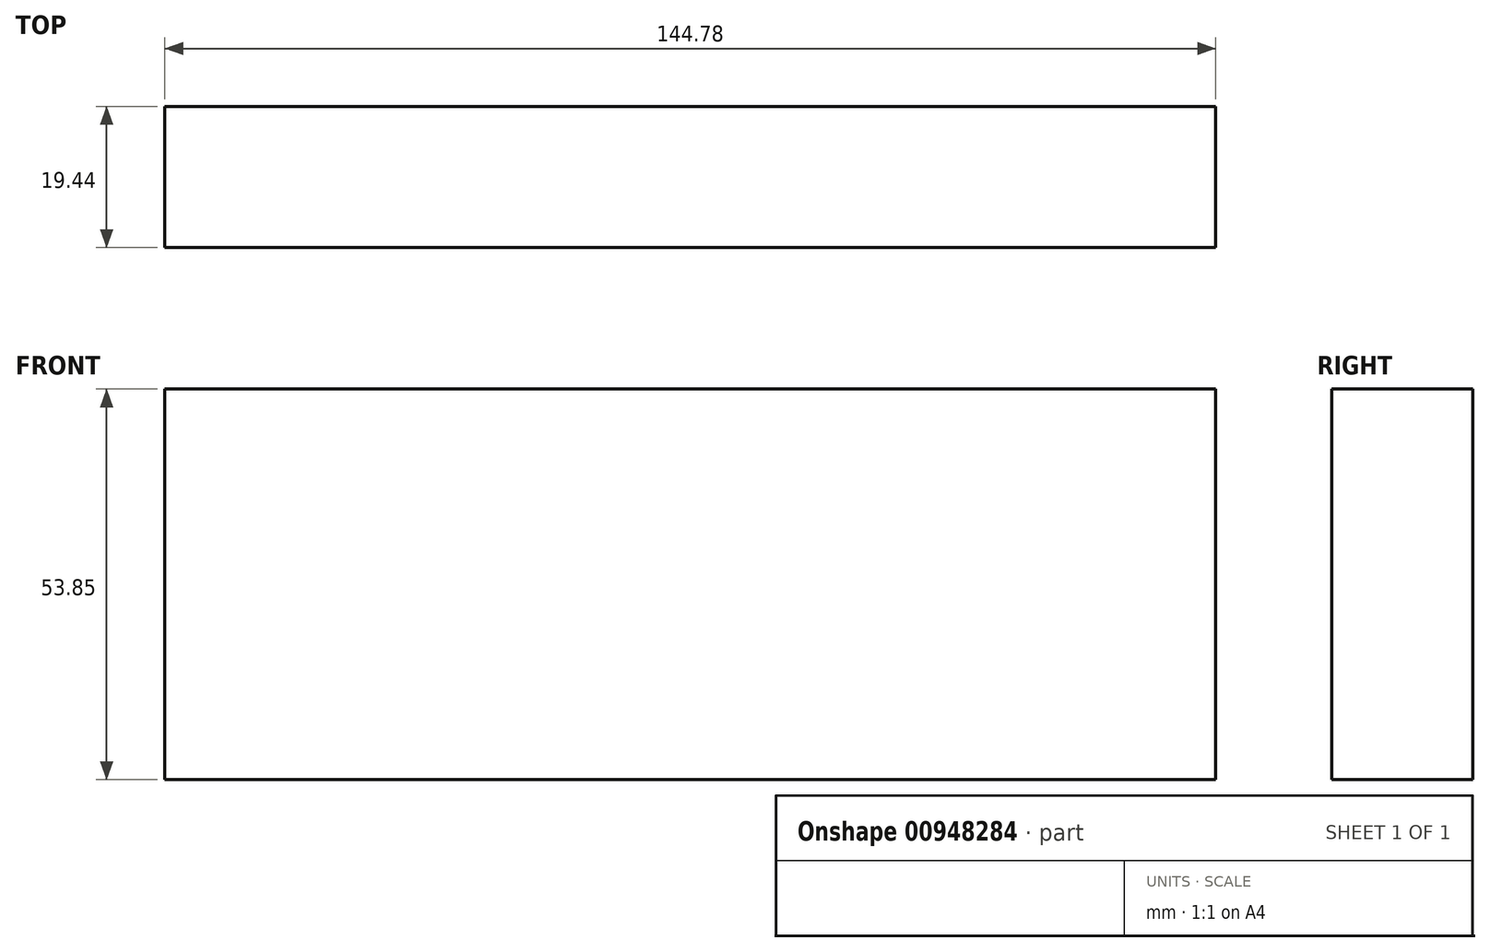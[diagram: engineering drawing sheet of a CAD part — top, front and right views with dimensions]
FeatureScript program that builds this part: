
annotation { "Feature Type Name" : "Feature", "Feature Type Description" : "" }
export const myFeature = defineFeature(function(context is Context, id is Id, definition is map)
    precondition{}
    {
        {
            var Q0;
            Q0=qCreatedBy(makeId("Top.planeOp"),FACE);
            var sketch = newSketch(context, id + "F0", { "sketchPlane" : qUnion([Q0])});
            skLineSegment(sketch, "E0.bottom", {"start": v(72.4, -9.72) * mm, "end": v(-72.4, -9.72) * mm});
            skLineSegment(sketch, "E0.top", {"start": v(72.4, 9.72) * mm, "end": v(-72.4, 9.72) * mm});
            skLineSegment(sketch, "E0.left", {"start": v(72.4, -9.72) * mm, "end": v(72.4, 9.72) * mm});
            skLineSegment(sketch, "E0.right", {"start": v(-72.4, -9.72) * mm, "end": v(-72.4, 9.72) * mm});
            skPoint(sketch, "E0.middle", {"position": v(0, 0) * mm});
            skSolve(sketch);
        }
        {
            var Q0;
            Q0 = qSketchRegion(id + "F0", true);
            extrude(context, id + "F1", {"entities" : qUnion([Q0]), "depth" : 53.85 * mm, "offsetDistance" : 25.4 * mm});
        }
    });
